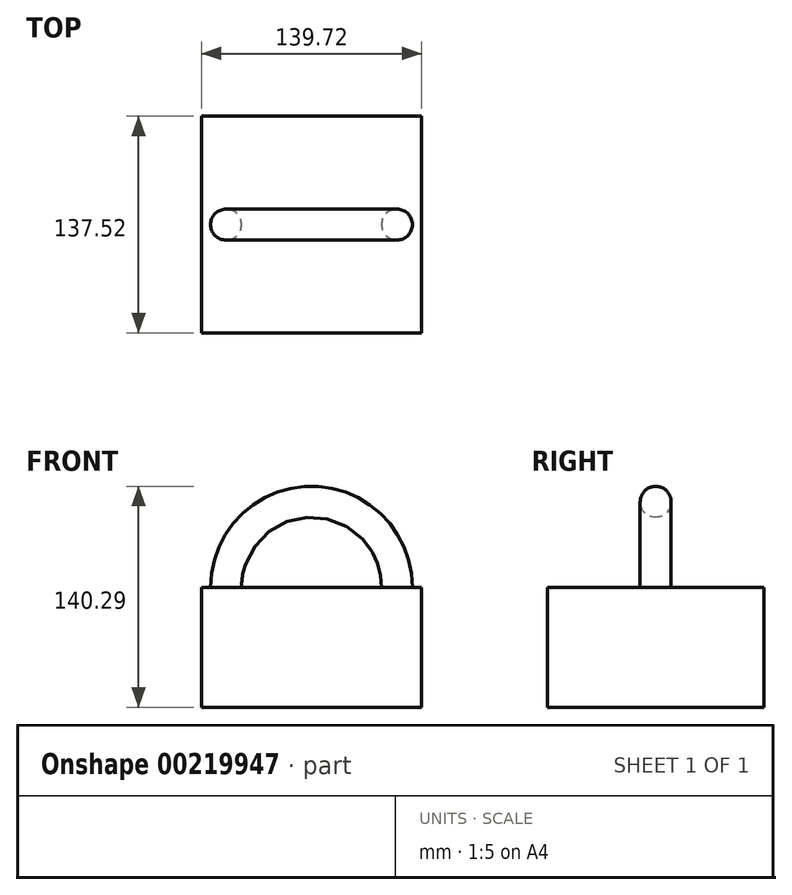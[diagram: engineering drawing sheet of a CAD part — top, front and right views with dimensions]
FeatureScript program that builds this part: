
annotation { "Feature Type Name" : "Feature", "Feature Type Description" : "" }
export const myFeature = defineFeature(function(context is Context, id is Id, definition is map)
    precondition{}
    {
        {
            var Q0;
            Q0=qCreatedBy(makeId("Top.planeOp"),FACE);
            var sketch = newSketch(context, id + "F0", { "sketchPlane" : qUnion([Q0])});
            skLineSegment(sketch, "E0.bottom", {"start": v(69.86, -68.76) * mm, "end": v(-69.86, -68.76) * mm});
            skLineSegment(sketch, "E0.top", {"start": v(69.86, 68.76) * mm, "end": v(-69.86, 68.76) * mm});
            skLineSegment(sketch, "E0.left", {"start": v(69.86, -68.76) * mm, "end": v(69.86, 68.76) * mm});
            skLineSegment(sketch, "E0.right", {"start": v(-69.86, -68.76) * mm, "end": v(-69.86, 68.76) * mm});
            skPoint(sketch, "E0.middle", {"position": v(0, 0) * mm});
            skLineSegment(sketch, "E1", {"start": v(0, 68.76) * mm, "end": v(0, -68.76) * mm});
            skSolve(sketch);
        }
        {
            var Q0;
            Q0=qCreatedBy(makeId("Top.planeOp"),FACE);
            var sketch = newSketch(context, id + "F1", { "sketchPlane" : qUnion([Q0])});
            skCircle(sketch, "E2", {"center": v(54.26, 0) * mm, "radius": 9.82 * mm});
            skSolve(sketch);
        }
        {
            var Q0;
            {var subQ0=sQuery(id+"F0.wireOp",EDGE,"E0.left");Q0=makeQuery(id+"F0.imprint","IMPRINT",FACE,{"disambiguationData":[TD([[makeQuery(id+"F0.imprint","IMPRINT",EDGE,{"derivedFrom":subQ0}),1.0]])]});}
            var Q1;
            {var subQ0=sQuery(id+"F0.wireOp",EDGE,"E0.right");Q1=makeQuery(id+"F0.imprint","IMPRINT",FACE,{"disambiguationData":[TD([[makeQuery(id+"F0.imprint","IMPRINT",EDGE,{"derivedFrom":subQ0}),-1.0]])]});}
            extrude(context, id + "F2", {"entities" : qUnion([Q0, Q1]), "oppositeDirection" : true, "depth" : 76.2 * mm});
        }
        {
            var Q0;
            Q0=makeQuery(id+"F1.imprint","IMPRINT",FACE,{"disambiguationData":[TD([[makeQuery(id+"F1.imprint","IMPRINT",EDGE,{"derivedFrom":sQuery(id+"F1.wireOp",EDGE,"E2")}),1.0]])]});
            var Q1;
            Q1=sQuery(id+"F0.wireOp",EDGE,"E1");
            revolve(context, id + "F3", {"operationType" : NewBodyOperationType.ADD, "entities" : qUnion([Q0]), "axis" : qUnion([Q1]), "revolveType" : RevolveType.ONE_DIRECTION, "angle" : 180 * degree});
        }
    });
